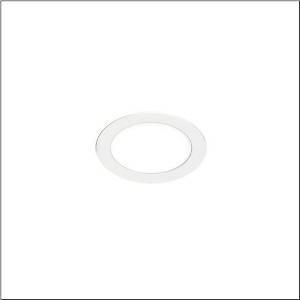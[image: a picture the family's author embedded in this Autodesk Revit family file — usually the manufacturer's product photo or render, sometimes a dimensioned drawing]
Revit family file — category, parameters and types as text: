
# Revit family: lunis_41_flat_51dr10mdgbb
name_source: partatom
category: Lighting Fixtures
units: mm (PartAtom-declared; Revit-internal decimal feet)

## family parameters
Cut with Voids When Loaded = No
Host = Face
Light Source = No
Part Type = Normal
Room Calculation Point = No
Round Connector Dimension = Use Diameter
Shared = No

## types (1)
- --- (1 x LED, 1580 lm, 12.5 W, 4000K)
    Apparent Load = 13 VA
    CIE Flux Codes = 49 80 96 100 100
    Color Rendering = 80
    Color Temperature = 4000K
    Default Elevation = 1800 mm
    Description = Lunis 41 Flat, downlight, light emission: direct distribution, LED rated luminous flux: 1.530lm, light colour: 830/840, mains connection: 230V, AC, 50/60Hz, housing, round, of aluminium, coated, traffic white (RAL 9016), diameter: 170mm, protection rating (complete): IP20, protection rating (on room side): IP44, insulation class (complete): insulation class II (safety insulation), certification: CE, permissible ambient temperature for indoor applications: -20..+40°C, packaging unit: 1 piece
    Height = 0 mm  [stored 0 ft]
    Lamp = 1 x LED
    Lamp Light Flux = 1580 lm
    Lamp Power = 12.5 W
    Lamp count = 1
    Length = 170 mm  [stored 0.557743 ft]
    Luminous efficacy = 126 lm/W
    Manufacturer = Siteco
    ModVariant = No
    Model = 51DR10MDGBB
    Mounting Place = Ceiling
    Mounting Type = Recessed
    Number of Poles = 1
    OnlyDefault = Yes
    Power Factor = 1
    Product Name = Lunis 41 Flat
    Product group = downlight
    ProductGroupID = 401
    Protection Class = Protection class II
    Protection Degree = IP 20
    RLX_Detail_Level = 1
    RLX_Emergency_Light_Flux = 0 lm
    RLX_Emergency_Type = 0
    RLX_Emergency_Type_DB = No
    RlxData = <blob elided: 9777 chars, md5=3f743b06>
    Socket = socket
    Standby Power = 0 W
    System Light Flux = 1580 lm
    System Power = 13 W
    Type Comments = factory setting: colour temperature 4000K
    Type Image = l_1340921.jpg
    URL = http://relux.com
    VarID = @adj_020041
    Voltage = 0 V
    Weight = 0.00 kg
    Width = 0 mm  [stored 0 ft]

note: [stored X ft] marks values corroborated as IEEE doubles in the binary element streams (Revit-internal decimal feet)

## geometry (parser evidence)
native form markers: Sweep x8
no freeform markers — native parametric forms only
